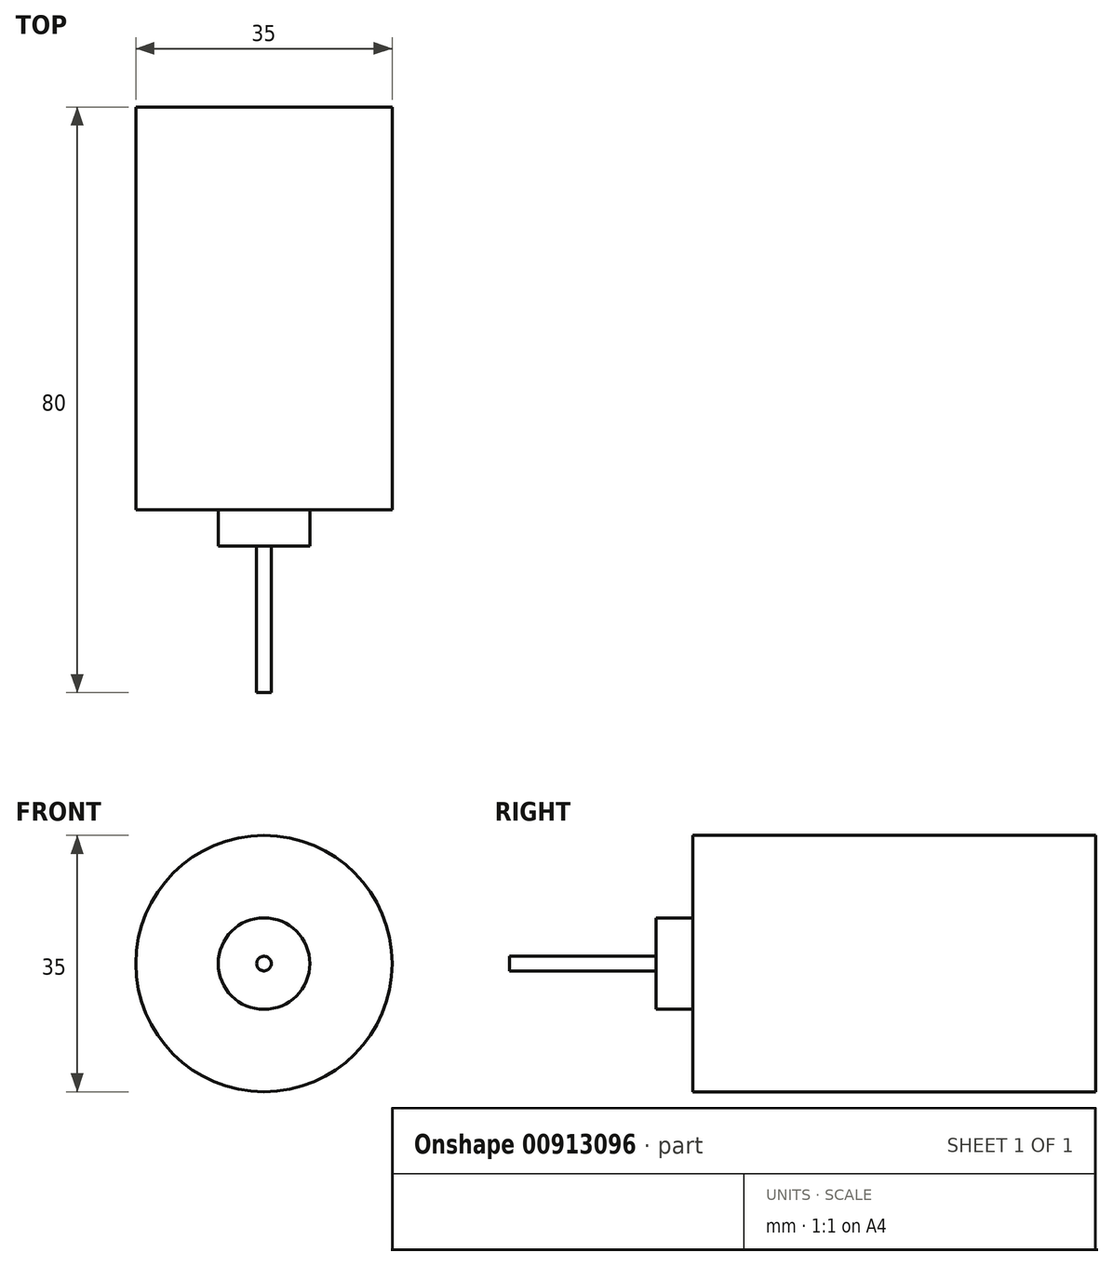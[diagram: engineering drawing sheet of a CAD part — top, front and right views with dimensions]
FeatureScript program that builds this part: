
annotation { "Feature Type Name" : "Feature", "Feature Type Description" : "" }
export const myFeature = defineFeature(function(context is Context, id is Id, definition is map)
    precondition{}
    {
        {
            var Q0;
            Q0=qCreatedBy(makeId("Front.planeOp"),FACE);
            var sketch = newSketch(context, id + "F0", { "sketchPlane" : qUnion([Q0])});
            skCircle(sketch, "E0", {"center": v(0, 0) * mm, "radius": 1 * mm});
            skSolve(sketch);
        }
        {
            var Q0;
            Q0 = qSketchRegion(id + "F0", true);
            extrude(context, id + "F1", {"entities" : qUnion([Q0]), "depth" : 20 * mm, "offsetDistance" : 25 * mm});
        }
        {
            var Q0;
            Q0=qCreatedBy(makeId("Front.planeOp"),FACE);
            var sketch = newSketch(context, id + "F2", { "sketchPlane" : qUnion([Q0])});
            skCircle(sketch, "E1", {"center": v(0, 0) * mm, "radius": 6.25 * mm});
            skSolve(sketch);
        }
        {
            var Q0;
            Q0=makeQuery(id+"F2.imprint","IMPRINT",FACE,{"disambiguationData":[TD([[makeQuery(id+"F2.imprint","IMPRINT",EDGE,{"derivedFrom":sQuery(id+"F2.wireOp",EDGE,"E1")}),1.0]])]});
            extrude(context, id + "F3", {"entities" : qUnion([Q0]), "operationType" : NewBodyOperationType.ADD, "oppositeDirection" : true, "depth" : 5 * mm, "offsetDistance" : 25 * mm});
        }
        {
            var Q0;
            Q0=qCreatedBy(makeId("Front.planeOp"),FACE);
            cPlane(context, id + "F4", {"entities" : qUnion([Q0]), "cplaneType" : CPlaneType.OFFSET, "offset" : 5 * mm, "oppositeDirection" : true, "width" : 150 * mm, "height" : 150 * mm});
        }
        {
            var Q0;
            Q0=qCreatedBy(id+"F4.planeOp",FACE);
            var sketch = newSketch(context, id + "F5", { "sketchPlane" : qUnion([Q0])});
            skCircle(sketch, "E2", {"center": v(0, 0) * mm, "radius": 17.5 * mm});
            skSolve(sketch);
        }
        {
            var Q0;
            Q0 = qSketchRegion(id + "F5", true);
            extrude(context, id + "F6", {"entities" : qUnion([Q0]), "operationType" : NewBodyOperationType.ADD, "oppositeDirection" : true, "depth" : 55 * mm, "offsetDistance" : 25 * mm});
        }
    });
